# Revit family: Forniture_Stools_Plank_Miura-Stool
name_source: partatom
category: Furniture
revit_build: Autodesk Revit 2017 (Build: 20160225_1515(x64)
units: mm (PartAtom-declared; Revit-internal decimal feet)

## family parameters
Cut with Voids When Loaded = No
Host = Face
Room Calculation Point = No
Shared = No

## types (1)
- Miura Stool-Mod. 8200-00
    BIMobject category = Chairs, Stools & Benches
    BIMobject category code = furniture-chairs-stools-benches
    BIMobject main category = Furniture
    BIMobject main category code = furniture
    Brand url = http://www.plank.it
    Default Elevation = 1219 mm
    Design country = Italy
    Edition number = 1
    IFC Classification = Furnishing Element
    Link model = https://www.plank.it
    Manufacturer country = Italy
    Manufacturer name = PLANK
    Masterformat 2014 Code = 12 00 00
    Masterformat 2014 Description = Furnishings
    Material main = Polypropylene
    Model = Miura Stool-Mod. 8200-00
    NBS Reference Code = 31
    NBS Reference Description = Fittings, Furnishings And Equipment (Ff&E) Products
    Nominal height = 810 mm
    Nominal width = 470 mm  [stored 1.54199 ft]
    OmniClass Code = 23-21 00 00
    OmniClass Description = Furnishings, Fixtures and Equipment Products
    Product Guid = 0742837d-7383-42c8-93dc-15da8bcf1d5d
    Product SKU = MIURA-Stool
    Product data url = https://bimobject.com
    Product family = Miura
    Product group = Stool
    Product url = https://www.plank.it
    QR code = http://bimobject.com
    Technical description = https://www.plank.it
    UNSPSC Code = 56
    URL = https://www.plank.it
    Uniclass 1.4 Code = JN
    Uniclass 1.4 Description = Furniture/Equipment
    Uniclass 2.0 Code = EE-35
    Uniclass 2.0 Description = Fittings, Furnishings And Equipment (Ff&E) And Signage Elements
    Uniclass 2015 Code = EF_40_30
    Uniclass 2015 Name = Furnishings
    Uniformat II Code = E2020
    Uniformat II Description = Movable Furnishings
    Weight Net (Kg) = 0
    stool = Plank- Red

note: [stored X ft] marks values corroborated as IEEE doubles in the binary element streams (Revit-internal decimal feet)
